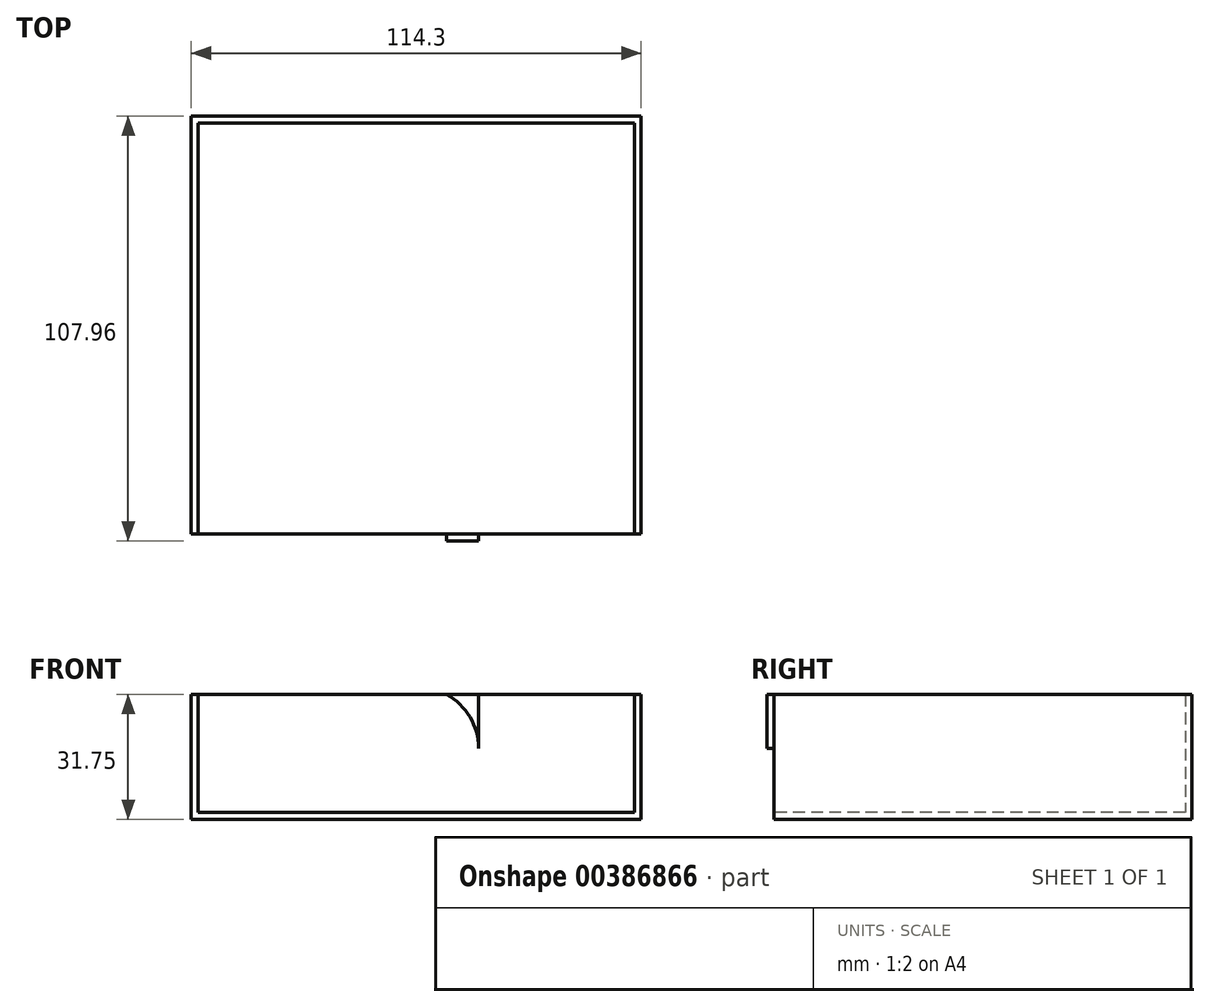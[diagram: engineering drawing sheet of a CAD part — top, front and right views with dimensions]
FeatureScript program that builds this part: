
annotation { "Feature Type Name" : "Feature", "Feature Type Description" : "" }
export const myFeature = defineFeature(function(context is Context, id is Id, definition is map)
    precondition{}
    {
        {
            var Q0;
            Q0=qCreatedBy(makeId("Top.planeOp"),FACE);
            var sketch = newSketch(context, id + "F0", { "sketchPlane" : qUnion([Q0])});
            skLineSegment(sketch, "E0.bottom", {"start": v(57.15, 53.98) * mm, "end": v(-57.15, 53.98) * mm});
            skLineSegment(sketch, "E0.top", {"start": v(57.15, -53.97) * mm, "end": v(-57.15, -53.97) * mm});
            skLineSegment(sketch, "E0.left", {"start": v(57.15, 53.98) * mm, "end": v(57.15, -53.97) * mm});
            skLineSegment(sketch, "E0.right", {"start": v(-57.15, 53.98) * mm, "end": v(-57.15, -53.97) * mm});
            skPoint(sketch, "E0.middle", {"position": v(0, 0) * mm});
            skSolve(sketch);
        }
        {
            var Q0;
            Q0=makeQuery(id+"F0.imprint","IMPRINT",FACE,{"disambiguationData":[TD([[makeQuery(id+"F0.imprint","IMPRINT",EDGE,{"derivedFrom":sQuery(id+"F0.wireOp",EDGE,"E0.bottom")}),1.0]])]});
            extrude(context, id + "F1", {"entities" : qUnion([Q0]), "depth" : 31.75 * mm});
        }
        {
            var Q0;
            Q0=makeQuery(id+"F1.opExtrude","SWEPT_FACE",FACE,{"disambiguationData":[OSD([sQuery(id+"F0.wireOp",EDGE,"E0.top")])]});
            var sketch = newSketch(context, id + "F2", { "sketchPlane" : qUnion([Q0])});
            skCircle(sketch, "E1", {"center": v(0, 17.88) * mm, "radius": 15.88 * mm});
            skLineSegment(sketch, "E2", {"start": v(15.87, 17.65) * mm, "end": v(15.87, 31.75) * mm});
            skLineSegment(sketch, "E3", {"start": v(-15.87, 17.65) * mm, "end": v(-16.07, 31.75) * mm});
            skSolve(sketch);
        }
        {
            var Q0;
            Q0=makeQuery(id+"F1.opExtrude","CAP_FACE",FACE,{"disambiguationData":[OSD([sQuery(id+"F0.wireOp",EDGE,"E0.bottom"),sQuery(id+"F0.wireOp",EDGE,"E0.top"),sQuery(id+"F0.wireOp",EDGE,"E0.left"),sQuery(id+"F0.wireOp",EDGE,"E0.right")])],"isStart":false});
            shell(context, id + "F3", {"entities" : qUnion([Q0]), "thickness" : 1.75 * mm});
        }
        {
            var Q0;
            Q0 = qSketchRegion(id + "F2", true);
            var Q1;
            {var subQ0=sQuery(id+"F2.wireOp",EDGE,"E3");Q1=makeQuery(id+"F2.imprint","IMPRINT",FACE,{"disambiguationData":[TD([[makeQuery(id+"F2.imprint","IMPRINT",EDGE,{"derivedFrom":subQ0}),-1.0]])]});}
            var Q2;
            {var subQ0=sQuery(id+"F2.wireOp",EDGE,"E2");var subQ1=sQuery(id+"F2.wireOp",EDGE,"E1");var subQ2=makeQuery(id+"F2.imprint","INTERSECT",VERTEX,{"disambiguationData":[OD(1.0)],"derivedFrom":[subQ1,subQ0]});Q2=makeQuery(id+"F2.imprint","IMPRINT",FACE,{"disambiguationData":[TD([[makeQuery(id+"F2.imprint","IMPRINT",EDGE,{"disambiguationData":[TD([[subQ2,-1.0]])],"derivedFrom":subQ1}),-1.0]])]});}
            extrude(context, id + "F4", {"entities" : qUnion([Q0, Q1, Q2]), "operationType" : NewBodyOperationType.REMOVE, "oppositeDirection" : true, "depth" : 1.75 * mm});
        }
    });
